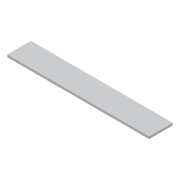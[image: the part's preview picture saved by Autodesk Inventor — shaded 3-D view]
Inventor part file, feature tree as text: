
AUTODESK INVENTOR PART (.ipt)
format: ipt  version: 2016 (Build 200138000, 138)  size: 66,048 bytes
history: native  units: mm
features: extrude x1, sketch x1
ambient origin geometry x8: Origin, YZ Plane, XZ Plane, XY Plane, X Axis, Y Axis, Z Axis, Center Point
bodies: Volumenkörper1 (feature_tree)
feature tree (2):
  extrude  "Extrusion1"  Depth=100.0mm
  sketch  "Skizze1"  dims[d2=10.0mm d3=0.0mm d4=100.0mm d5=600.0mm]
